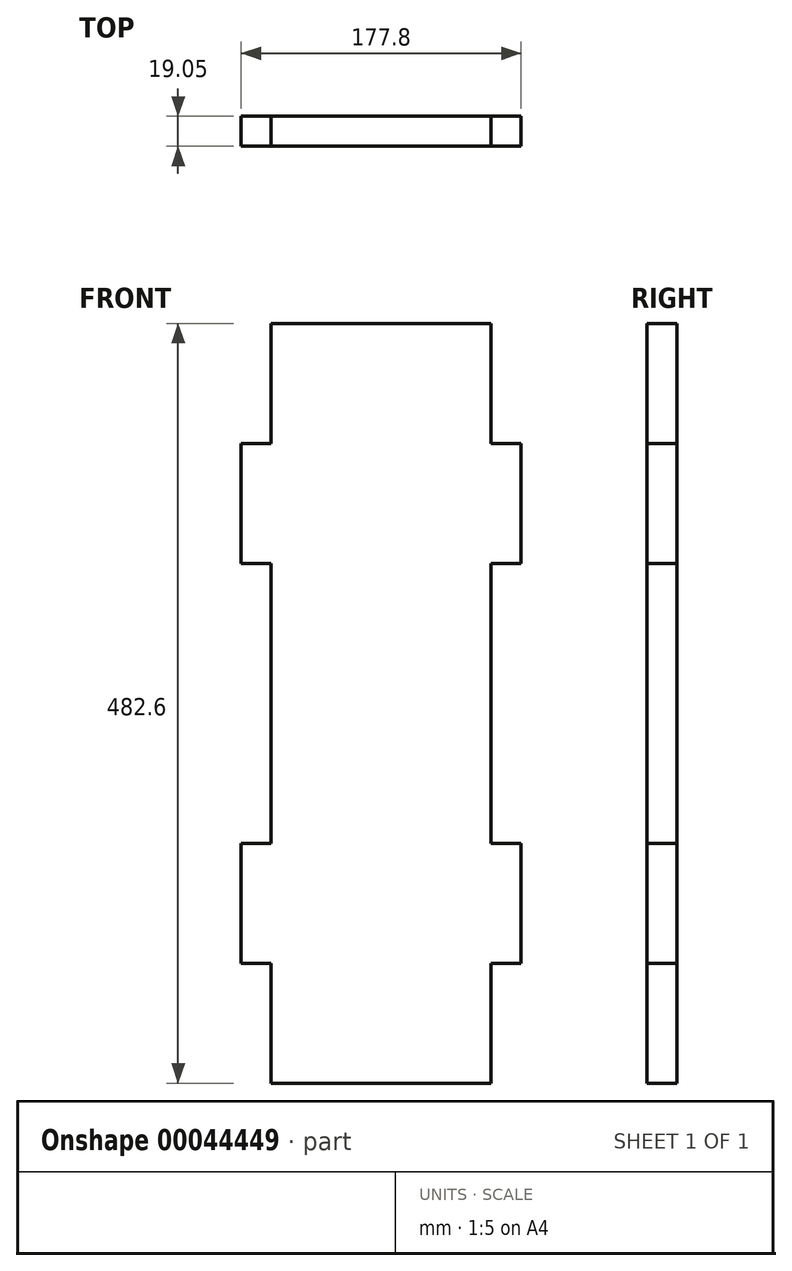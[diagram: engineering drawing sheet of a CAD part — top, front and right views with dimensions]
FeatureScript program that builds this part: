
annotation { "Feature Type Name" : "Feature", "Feature Type Description" : "" }
export const myFeature = defineFeature(function(context is Context, id is Id, definition is map)
    precondition{}
    {
        {
            var Q0;
            Q0=qCreatedBy(makeId("Front.planeOp"),FACE);
            var sketch = newSketch(context, id + "F0", { "sketchPlane" : qUnion([Q0])});
            skLineSegment(sketch, "E0.bottom", {"start": v(-69.85, 171.45) * mm, "end": v(69.85, 171.45) * mm});
            skLineSegment(sketch, "E0.top", {"start": v(-69.85, -158.75) * mm, "end": v(69.85, -158.75) * mm});
            skLineSegment(sketch, "E0.left", {"start": v(-69.85, 171.45) * mm, "end": v(-69.85, -158.75) * mm});
            skLineSegment(sketch, "E0.right", {"start": v(69.85, 171.45) * mm, "end": v(69.85, -158.75) * mm});
            skLineSegment(sketch, "E1.bottom", {"start": v(69.85, 171.45) * mm, "end": v(88.9, 171.45) * mm});
            skLineSegment(sketch, "E1.top", {"start": v(69.85, 95.25) * mm, "end": v(88.9, 95.25) * mm});
            skLineSegment(sketch, "E1.left", {"start": v(69.85, 171.45) * mm, "end": v(69.85, 95.25) * mm});
            skLineSegment(sketch, "E1.right", {"start": v(88.9, 171.45) * mm, "end": v(88.9, 95.25) * mm});
            skLineSegment(sketch, "E2.bottom", {"start": v(-69.85, 171.45) * mm, "end": v(-88.9, 171.45) * mm});
            skLineSegment(sketch, "E2.top", {"start": v(-69.85, 95.25) * mm, "end": v(-88.9, 95.25) * mm});
            skLineSegment(sketch, "E2.left", {"start": v(-69.85, 171.45) * mm, "end": v(-69.85, 95.25) * mm});
            skLineSegment(sketch, "E2.right", {"start": v(-88.9, 171.45) * mm, "end": v(-88.9, 95.25) * mm});
            skLineSegment(sketch, "E3.bottom", {"start": v(69.85, -158.75) * mm, "end": v(88.9, -158.75) * mm});
            skLineSegment(sketch, "E3.top", {"start": v(69.85, -82.55) * mm, "end": v(88.9, -82.55) * mm});
            skLineSegment(sketch, "E3.left", {"start": v(69.85, -158.75) * mm, "end": v(69.85, -82.55) * mm});
            skLineSegment(sketch, "E3.right", {"start": v(88.9, -158.75) * mm, "end": v(88.9, -82.55) * mm});
            skLineSegment(sketch, "E4.bottom", {"start": v(-69.85, -158.75) * mm, "end": v(-88.9, -158.75) * mm});
            skLineSegment(sketch, "E4.top", {"start": v(-69.85, -82.55) * mm, "end": v(-88.9, -82.55) * mm});
            skLineSegment(sketch, "E4.left", {"start": v(-69.85, -158.75) * mm, "end": v(-69.85, -82.55) * mm});
            skLineSegment(sketch, "E4.right", {"start": v(-88.9, -158.75) * mm, "end": v(-88.9, -82.55) * mm});
            skLineSegment(sketch, "E5", {"start": v(-69.85, 171.45) * mm, "end": v(-69.85, 247.65) * mm});
            skLineSegment(sketch, "E6", {"start": v(-69.85, 247.65) * mm, "end": v(69.85, 247.65) * mm});
            skLineSegment(sketch, "E7", {"start": v(69.85, 247.65) * mm, "end": v(69.85, 171.45) * mm});
            skLineSegment(sketch, "E8", {"start": v(-69.85, -158.75) * mm, "end": v(-69.85, -234.95) * mm});
            skLineSegment(sketch, "E9", {"start": v(-69.85, -234.95) * mm, "end": v(69.85, -234.95) * mm});
            skLineSegment(sketch, "E10", {"start": v(69.85, -234.95) * mm, "end": v(69.85, -158.75) * mm});
            skSolve(sketch);
        }
        {
            var Q0;
            Q0 = qSketchRegion(id + "F0", true);
            extrude(context, id + "F1", {"entities" : qUnion([Q0]), "depth" : 19.05 * mm});
        }
    });
